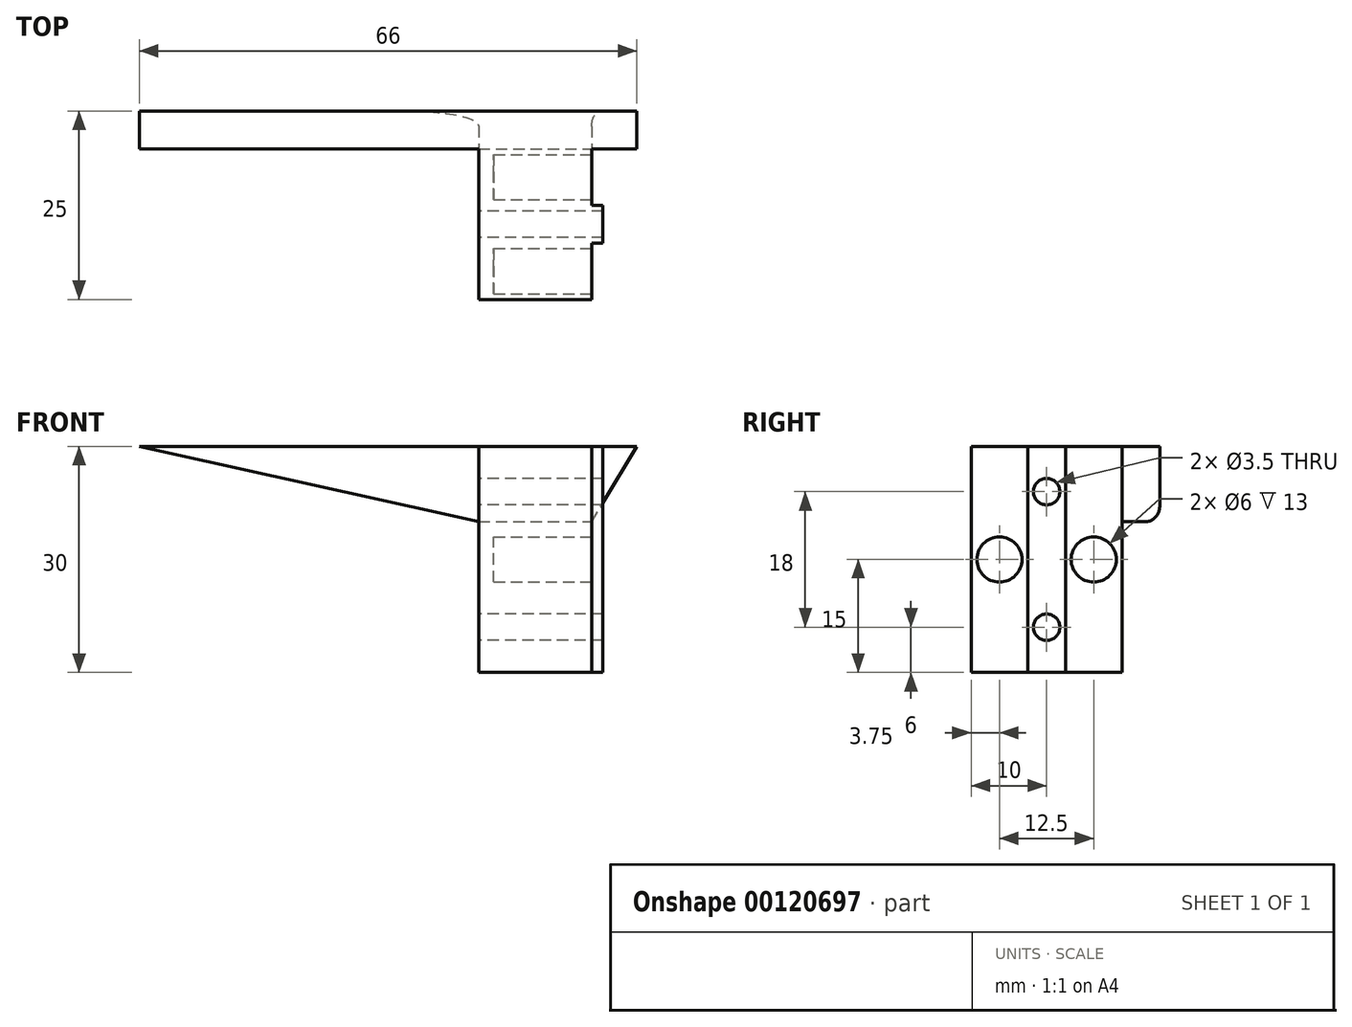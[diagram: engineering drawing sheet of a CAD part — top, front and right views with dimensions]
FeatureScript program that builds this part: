
annotation { "Feature Type Name" : "Feature", "Feature Type Description" : "" }
export const myFeature = defineFeature(function(context is Context, id is Id, definition is map)
    precondition{}
    {
        {
            var Q0;
            Q0=qCreatedBy(makeId("Top.planeOp"),FACE);
            var sketch = newSketch(context, id + "F0", { "sketchPlane" : qUnion([Q0])});
            skLineSegment(sketch, "E0", {"start": v(0, 0) * mm, "end": v(-15, 0) * mm});
            skLineSegment(sketch, "E1", {"start": v(-15, 0) * mm, "end": v(-15, -20) * mm});
            skLineSegment(sketch, "E2", {"start": v(-15, -20) * mm, "end": v(0, -20) * mm});
            skLineSegment(sketch, "E3", {"start": v(0, -20) * mm, "end": v(0, -12.5) * mm});
            skLineSegment(sketch, "E4", {"start": v(0, -12.5) * mm, "end": v(1.5, -12.5) * mm});
            skLineSegment(sketch, "E5", {"start": v(1.5, -12.5) * mm, "end": v(1.5, -7.5) * mm});
            skLineSegment(sketch, "E6", {"start": v(1.5, -7.5) * mm, "end": v(0, -7.5) * mm});
            skLineSegment(sketch, "E7", {"start": v(0, -7.5) * mm, "end": v(0, 0) * mm});
            skSolve(sketch);
        }
        {
            var Q0;
            Q0 = qSketchRegion(id + "F0", true);
            extrude(context, id + "F1", {"entities" : qUnion([Q0]), "depth" : 30 * mm});
        }
        {
            var Q0;
            Q0=makeQuery(id+"F1.opExtrude","SWEPT_FACE",FACE,{"disambiguationData":[OSD([sQuery(id+"F0.wireOp",EDGE,"E1")])]});
            var sketch = newSketch(context, id + "F2", { "sketchPlane" : qUnion([Q0])});
            skCircle(sketch, "E8", {"center": v(10, 24) * mm, "radius": 1.75 * mm});
            skPoint(sketch, "E8.centerSnap0", {"position": v(10, 30) * mm});
            skCircle(sketch, "E9", {"center": v(10, 6) * mm, "radius": 1.75 * mm});
            skSolve(sketch);
        }
        {
            var Q0;
            Q0 = qSketchRegion(id + "F2", true);
            extrude(context, id + "F3", {"entities" : qUnion([Q0]), "operationType" : NewBodyOperationType.REMOVE, "endBound" : BoundingType.THROUGH_ALL, "oppositeDirection" : true, "depth" : 25 * mm});
        }
        {
            var Q0;
            Q0=makeQuery(id+"F1.opExtrude","SWEPT_FACE",FACE,{"disambiguationData":[OSD([sQuery(id+"F0.wireOp",EDGE,"E3")])]});
            var sketch = newSketch(context, id + "F4", { "sketchPlane" : qUnion([Q0])});
            skCircle(sketch, "E10", {"center": v(-16.25, 15) * mm, "radius": 3 * mm});
            skPoint(sketch, "E10.centerSnap0", {"position": v(-16.25, 30) * mm});
            skPoint(sketch, "E10.centerSnap1", {"position": v(-20, 15) * mm});
            skSolve(sketch);
        }
        {
            var Q0;
            Q0 = qSketchRegion(id + "F4", true);
            extrude(context, id + "F5", {"entities" : qUnion([Q0]), "operationType" : NewBodyOperationType.REMOVE, "oppositeDirection" : true, "depth" : 13 * mm});
        }
        {
            var Q0;
            Q0=makeQuery(id+"F1.opExtrude","SWEPT_FACE",FACE,{"disambiguationData":[OSD([sQuery(id+"F0.wireOp",EDGE,"E7")])]});
            var sketch = newSketch(context, id + "F6", { "sketchPlane" : qUnion([Q0])});
            skCircle(sketch, "E11", {"center": v(-3.75, 15) * mm, "radius": 3 * mm});
            skPoint(sketch, "E11.centerSnap0", {"position": v(-3.75, 30) * mm});
            skPoint(sketch, "E11.centerSnap1", {"position": v(-7.5, 15) * mm});
            skSolve(sketch);
        }
        {
            var Q0;
            Q0 = qSketchRegion(id + "F6", true);
            extrude(context, id + "F7", {"entities" : qUnion([Q0]), "operationType" : NewBodyOperationType.REMOVE, "oppositeDirection" : true, "depth" : 13 * mm});
        }
        {
            var Q0;
            Q0=makeQuery(id+"F1.opExtrude","SWEPT_FACE",FACE,{"disambiguationData":[OSD([sQuery(id+"F0.wireOp",EDGE,"E0")])]});
            var sketch = newSketch(context, id + "F8", { "sketchPlane" : qUnion([Q0])});
            skLineSegment(sketch, "E12", {"start": v(15, 30) * mm, "end": v(60, 30) * mm});
            skLineSegment(sketch, "E13", {"start": v(60, 30) * mm, "end": v(15, 20) * mm});
            skLineSegment(sketch, "E14", {"start": v(15, 20) * mm, "end": v(0, 20) * mm});
            skLineSegment(sketch, "E15", {"start": v(0, 20) * mm, "end": v(-6, 30) * mm});
            skLineSegment(sketch, "E16", {"start": v(-6, 30) * mm, "end": v(15, 30) * mm});
            skSolve(sketch);
        }
        {
            var Q0;
            Q0 = qSketchRegion(id + "F8", true);
            extrude(context, id + "F9", {"entities" : qUnion([Q0]), "operationType" : NewBodyOperationType.ADD, "depth" : 5 * mm});
        }
        {
            var Q0;
            Q0=makeQuery(id+"F9.opExtrude","CAP_EDGE",EDGE,{"disambiguationData":[OSD([sQuery(id+"F8.wireOp",EDGE,"E14")])],"isStart":true});
            var Q1;
            Q1=makeQuery(id+"F9.opExtrude","CAP_EDGE",EDGE,{"disambiguationData":[OSD([sQuery(id+"F8.wireOp",EDGE,"E14")])],"isStart":false});
            fillet(context, id + "F10", {"entities" : qUnion([Q0, Q1]), "radius" : 2 * mm, "tangentPropagation" : true, "allowEdgeOverflow" : false});
        }
    });
